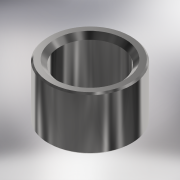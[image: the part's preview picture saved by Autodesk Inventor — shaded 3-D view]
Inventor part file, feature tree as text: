
AUTODESK INVENTOR PART (.ipt)
format: ipt  version: 2017 (Build 210142000, 142)  size: 132,608 bytes
history: native  units: mm
features: chamfer x2, extrude x1, sketch x1
ambient origin geometry x8: Origin, YZ Plane, XZ Plane, XY Plane, X Axis, Y Axis, Z Axis, Center Point
bodies: Solid1 (feature_tree)
feature tree (4):
  extrude  "Extrusion1"  Depth=7.0mm
  chamfer  "Chamfer1"  Distance=7.0mm
  chamfer  "Chamfer2"  Distance=0.6mm Angle=45.0deg
  sketch  "Sketch1"  dims[d0=11.0mm d1=8.0mm d2=7.0mm d3=0.0mm d4=0.6mm d5=2.0mm d6=45.0deg d7=0.2mm d8=2.0mm d9=45.0deg]
